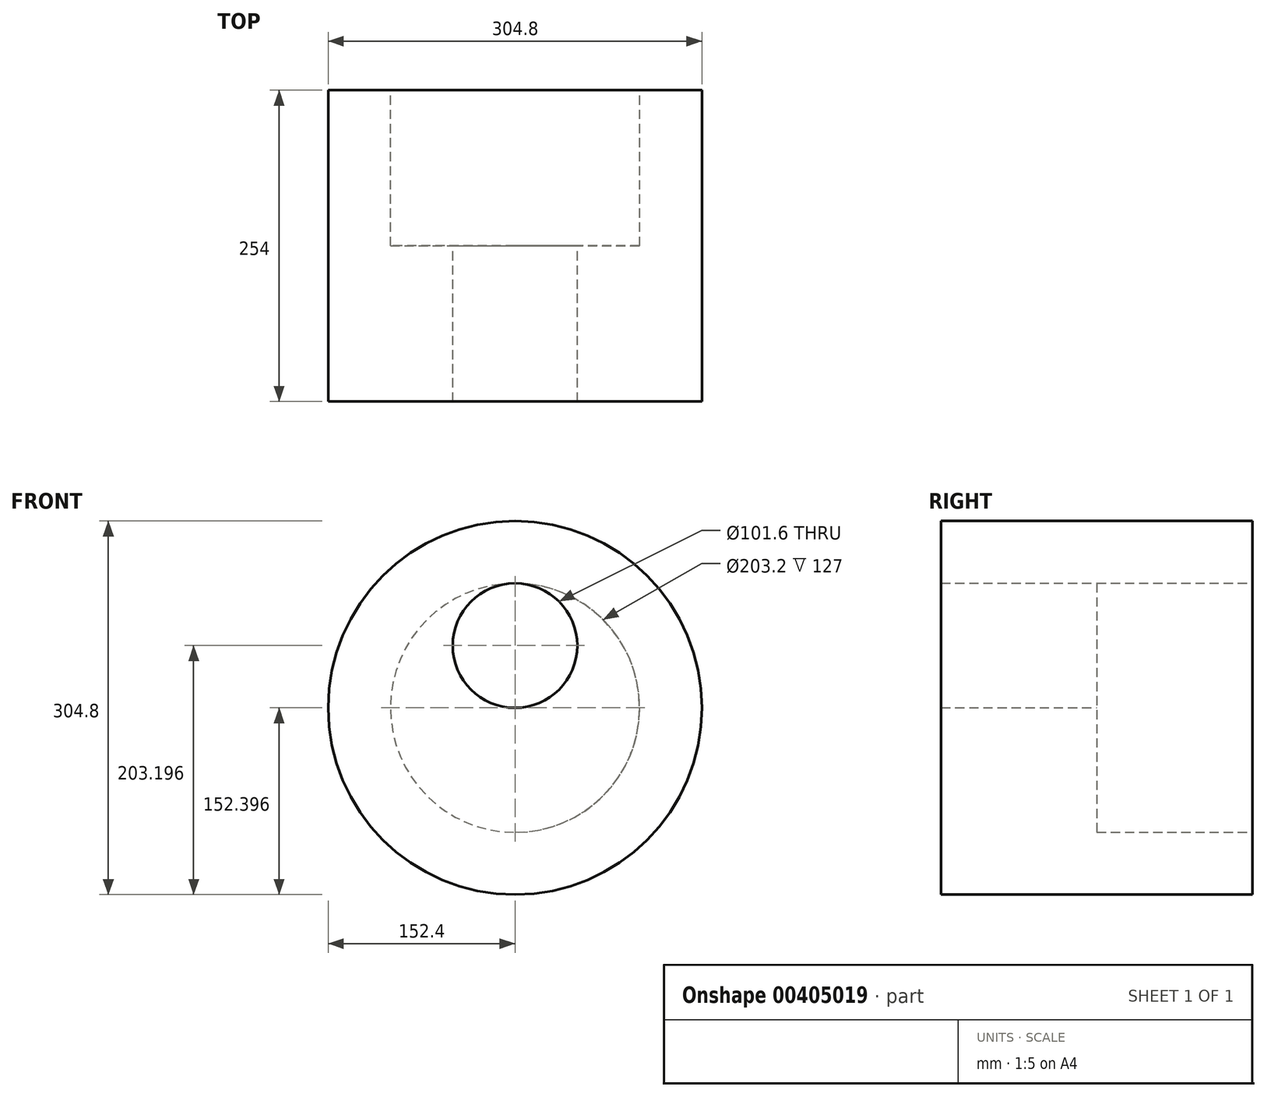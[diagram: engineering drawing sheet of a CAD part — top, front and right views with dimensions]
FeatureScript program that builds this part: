
annotation { "Feature Type Name" : "Feature", "Feature Type Description" : "" }
export const myFeature = defineFeature(function(context is Context, id is Id, definition is map)
    precondition{}
    {
        {
            var Q0;
            Q0=qCreatedBy(makeId("Front.planeOp"),FACE);
            var sketch = newSketch(context, id + "F0", { "sketchPlane" : qUnion([Q0])});
            skCircle(sketch, "E0", {"center": v(0, 0) * mm, "radius": 0.8 * mm});
            skCircle(sketch, "E1", {"center": v(0, -0.8) * mm, "radius": 1.59 * mm});
            skCircle(sketch, "E2", {"center": v(0, -0.8) * mm, "radius": 50.8 * mm});
            skCircle(sketch, "E3", {"center": v(0, -51.6) * mm, "radius": 101.6 * mm});
            skCircle(sketch, "E4", {"center": v(0, -51.6) * mm, "radius": 152.4 * mm});
            skSolve(sketch);
        }
        {
            var Q0;
            Q0=makeQuery(id+"F0.imprint","IMPRINT",FACE,{"disambiguationData":[TD([[makeQuery(id+"F0.imprint","IMPRINT",EDGE,{"derivedFrom":sQuery(id+"F0.wireOp",EDGE,"E3")}),-1.0]])]});
            var Q1;
            Q1=makeQuery(id+"F0.imprint","IMPRINT",FACE,{"disambiguationData":[TD([[makeQuery(id+"F0.imprint","IMPRINT",EDGE,{"derivedFrom":sQuery(id+"F0.wireOp",EDGE,"E2")}),-1.0]])]});
            extrude(context, id + "F1", {"entities" : qUnion([Q0, Q1]), "depth" : 254 * mm});
        }
        {
            var Q0;
            Q0=makeQuery(id+"F0.imprint","IMPRINT",FACE,{"disambiguationData":[TD([[makeQuery(id+"F0.imprint","IMPRINT",EDGE,{"derivedFrom":sQuery(id+"F0.wireOp",EDGE,"E2")}),-1.0]])]});
            var Q1;
            Q1=makeQuery(id+"F0.imprint","IMPRINT",FACE,{"disambiguationData":[TD([[makeQuery(id+"F0.imprint","IMPRINT",EDGE,{"derivedFrom":sQuery(id+"F0.wireOp",EDGE,"E1")}),-1.0]])]});
            var Q2;
            Q2=sQuery(id+"F0.wireOp",EDGE,"E3");
            extrude(context, id + "F2", {"entities" : qUnion([Q0, Q1]), "operationType" : NewBodyOperationType.REMOVE, "surfaceEntities" : qUnion([Q2]), "depth" : 127 * mm});
        }
    });
